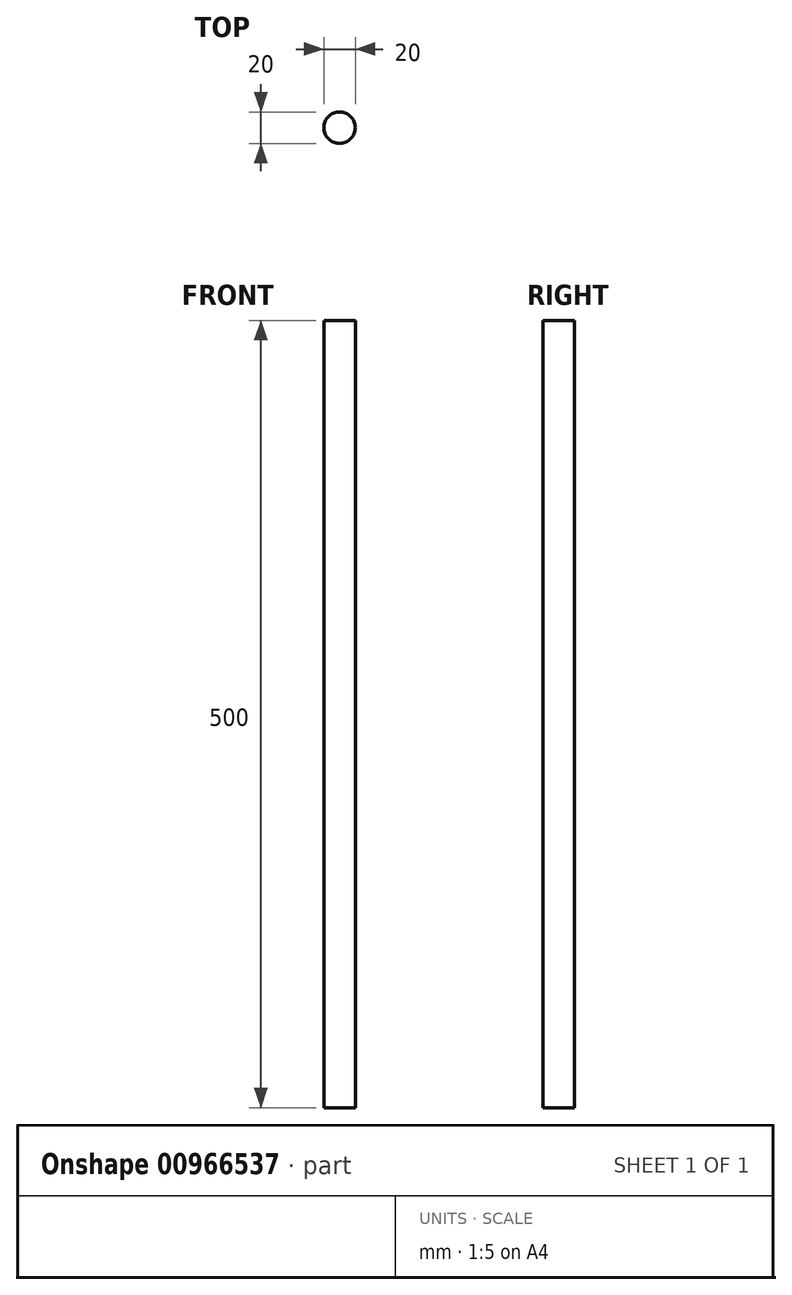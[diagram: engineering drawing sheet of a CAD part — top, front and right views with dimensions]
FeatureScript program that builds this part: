
annotation { "Feature Type Name" : "Feature", "Feature Type Description" : "" }
export const myFeature = defineFeature(function(context is Context, id is Id, definition is map)
    precondition{}
    {
        {
            var Q0;
            Q0=qCreatedBy(makeId("Top.planeOp"),FACE);
            var sketch = newSketch(context, id + "F0", { "sketchPlane" : qUnion([Q0])});
            skCircle(sketch, "E0", {"center": v(0, 0) * mm, "radius": 10 * mm});
            skSolve(sketch);
        }
        {
            var Q0;
            Q0 = qSketchRegion(id + "F0", true);
            extrude(context, id + "F1", {"entities" : qUnion([Q0]), "depth" : 500 * mm, "offsetDistance" : 25.4 * mm});
        }
    });
